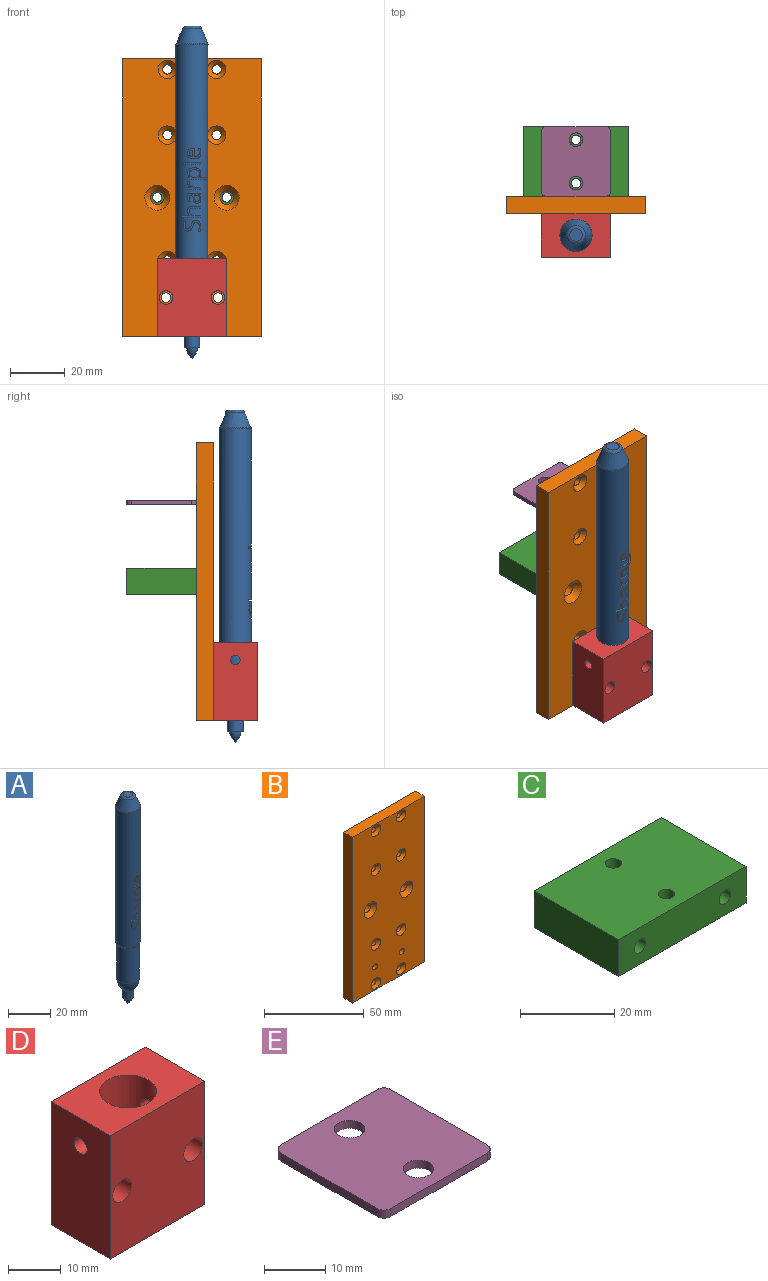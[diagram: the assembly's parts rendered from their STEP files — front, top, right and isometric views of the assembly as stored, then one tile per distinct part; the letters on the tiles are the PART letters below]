
ASSEMBLY  parts=5 mates=5
PART A: 161 faces, bbox 21x21x125.7 mm
  f0: cylinder r=5.87mm len=78.14mm, axis (0,0,-1), area 2809.1mm2, adj f9,f10,f11,f12,f13,f14,f15,f16
  f1: plane 13.84x13.84mm, normal (0,0,-1), area 11.1mm2, adj f2,f7
  f2: revolved ~4.13x2.06mm, area 0mm2, adj f1
  f3: plane 4.64x4.64mm, normal (0,0,1), area 16.9mm2, adj f8
  f4: cone r=5.87mm half-angle=22deg, axis (0,0,-1), area 177.5mm2, adj f8,f9
  f5: cylinder r=5.4mm len=20.32mm, axis (0,0,-1), area 689.1mm2, adj f6,f10
  f6: revolved ~10.8x10.8mm, area 199.6mm2, adj f5,f7
  f7: cylinder r=2.79mm len=5.59mm, axis (0,0,-1), area 83.6mm2, adj f1,f6
  f8: torus R=2.32mm, axis (0,0,1), area 28.3mm2, adj f3,f4
  f9: torus R=4.6mm, axis (0,0,1), area 17.9mm2, adj f0,f4
  f10: torus R=4.6mm, axis (0,0,-1), area 40.8mm2, adj f0,f5
  f11: plane 4.94x0.72mm, normal (-1,0,0), area 3.5mm2, adj f0,f12,f26,f28
  f12: plane 5.87x3.08mm, normal (0,0,-1), area 17.1mm2, adj f0,f11,f13,f26
  f13: extruded ~5.87x1.31mm, area 8.2mm2, adj f0,f12,f14,f26
  f14: extruded ~5.75x1.3mm, area 7.9mm2, adj f0,f13,f15,f26
  f15: extruded ~5.7x0.89mm, area 5.2mm2, adj f0,f14,f16,f26
  f16: extruded ~5.81x0.6mm, area 4.7mm2, adj f0,f15,f17,f26
  f17: plane 5.81x0.04mm, normal (1,0,0), area 0.2mm2, adj f0,f16,f18,f26
  f18: extruded ~5.81x0.61mm, area 3.5mm2, adj f0,f17,f19,f26
  f19: plane 5.68x2.03mm, normal (0,0,-1), area 10.7mm2, adj f0,f18,f20,f26
  f20: plane 4.7x0.72mm, normal (1,0,0), area 3.4mm2, adj f0,f19,f21,f26
  f21: plane 6.7x5.87mm, normal (0,0,1), area 37.1mm2, adj f0,f20,f22,f26
  f22: plane 4.94x0.72mm, normal (-1,0,0), area 3.5mm2, adj f0,f21,f23,f26
  f23: plane 5.83x2.47mm, normal (0,0,-1), area 13.6mm2, adj f0,f22,f24,f26
  f24: extruded ~5.87x1.33mm, area 8.2mm2, adj f0,f23,f25,f26
  f25: extruded ~5.84x1.09mm, area 7mm2, adj f0,f24,f26,f27
  f26: plane 6.7x3.95mm, normal (0,-1,0), area 9.5mm2, adj f11,f12,f13,f14,f15,f16,f17,f18
  f27: extruded ~5.83x0.82mm, area 5.2mm2, adj f0,f25,f26,f29
  f28: plane 5.87x3.05mm, normal (0,0,1), area 17mm2, adj f0,f11,f26,f29
  f29: extruded ~5.87x0.86mm, area 5.4mm2, adj f0,f26,f27,f28
  f30: extruded ~5.71x0.81mm, area 4.9mm2, adj f0,f31,f40,f42
  f31: extruded ~5.84x0.71mm, area 5.5mm2, adj f0,f30,f32,f40
  f32: plane 5.84x0.03mm, normal (1,0,0), area 0.2mm2, adj f0,f31,f33,f40
  f33: plane 5.84x0.87mm, normal (0.09,0,-1), area 5.1mm2, adj f0,f32,f34,f40
  f34: plane 5.67x0.59mm, normal (1,0,0), area 3.3mm2, adj f0,f33,f35,f40
  f35: plane 5.87x4.72mm, normal (0,0,1), area 26.7mm2, adj f0,f34,f36,f40
  f36: plane 4.94x0.72mm, normal (-1,0,0), area 3.5mm2, adj f0,f35,f37,f40
  f37: plane 5.84x2.53mm, normal (0,0,-1), area 13.9mm2, adj f0,f36,f38,f40
  f38: extruded ~5.85x1.16mm, area 7.3mm2, adj f0,f37,f39,f40
  f39: extruded ~5.85x0.98mm, area 6.5mm2, adj f0,f38,f40,f41
  f40: plane 4.81x2.72mm, normal (0,-1,0), area 4.6mm2, adj f30,f31,f32,f33,f34,f35,f36,f37
  f41: extruded ~5.8x0.52mm, area 3mm2, adj f0,f39,f40,f43
  f42: extruded ~5.66x0.56mm, area 3.2mm2, adj f0,f30,f40,f43
  f43: plane 5.8x0.66mm, normal (-0.15,0,-0.99), area 3.8mm2, adj f0,f40,f41,f42
  f44: plane 5.87x4.72mm, normal (0,0,-1), area 26.7mm2, adj f0,f45,f46,f47
  f45: plane 4.72x0.72mm, normal (0,-1,0), area 3.4mm2, adj f44,f46,f47,f48
  f46: plane 5.67x0.72mm, normal (1,0,0), area 4.1mm2, adj f0,f44,f45,f48
  f47: plane 4.94x0.72mm, normal (-1,0,0), area 3.5mm2, adj f0,f44,f45,f48
  f48: plane 5.87x4.72mm, normal (0,0,1), area 26.7mm2, adj f0,f45,f46,f47
  f49: extruded ~5.33x0.36mm, area 2mm2, adj f0,f50,f54,f56
  f50: extruded ~5.39x0.3mm, area 1.8mm2, adj f0,f49,f51,f54
  f51: extruded ~5.39x0.3mm, area 1.8mm2, adj f0,f50,f52,f54
  f52: extruded ~5.33x0.36mm, area 2.1mm2, adj f0,f51,f53,f54
  f53: extruded ~5.15x0.36mm, area 2mm2, adj f0,f52,f54,f55
  f54: plane 0.95x0.84mm, normal (0,-1,0), area 0.7mm2, adj f49,f50,f51,f52,f53,f55,f56,f57
  f55: extruded ~4.94x0.3mm, area 1.6mm2, adj f0,f53,f54,f57
  f56: extruded ~5.15x0.36mm, area 2mm2, adj f0,f49,f54,f57
  f57: extruded ~4.94x0.3mm, area 1.6mm2, adj f0,f54,f55,f56
  f58: extruded ~5.33x0.66mm, area 3.7mm2, adj f59,f79,f81,f86
  f59: extruded ~5.57x0.59mm, area 3.6mm2, adj f58,f60,f79,f86
  f60: extruded ~5.76x0.73mm, area 4.9mm2, adj f59,f61,f79,f86
  f61: extruded ~5.81x1.23mm, area 7.4mm2, adj f60,f62,f79,f86
  f62: plane 5.81x0.72mm, normal (-1,0,-0.04), area 4.2mm2, adj f61,f79,f80,f86
  f63: plane 4.94x0.53mm, normal (-1,0,0), area 2.6mm2, adj f0,f64,f79,f84
  f64: plane 5.87x3.22mm, normal (0,0,-1), area 18mm2, adj f0,f63,f65,f79
  f65: extruded ~5.87x1.2mm, area 7.6mm2, adj f0,f64,f66,f79
  f66: extruded ~5.74x1.25mm, area 7.6mm2, adj f0,f65,f67,f79
  f67: extruded ~5.68x0.83mm, area 4.8mm2, adj f0,f66,f68,f79
  f68: extruded ~5.75x0.76mm, area 4.7mm2, adj f0,f67,f69,f79
  f69: plane 5.84x0.55mm, normal (-0.37,0,0.93), area 3.4mm2, adj f0,f68,f70,f79
  f70: extruded ~5.84x1.33mm, area 8.1mm2, adj f0,f69,f71,f79
  f71: extruded ~5.82x0.77mm, area 4.8mm2, adj f0,f70,f72,f79
  f72: extruded ~5.87x0.82mm, area 5.1mm2, adj f0,f71,f73,f79
  f73: plane 5.87x0.29mm, normal (0,0,1), area 1.7mm2, adj f0,f72,f74,f79
  f74: plane 5.86x0.8mm, normal (1,0,0.03), area 4.7mm2, adj f0,f73,f75,f79
  f75: extruded ~5.86x2.29mm, area 17.8mm2, adj f0,f74,f76,f79
  f76: extruded ~5.57x1.03mm, area 6.1mm2, adj f0,f75,f77,f79
  f77: extruded ~5.11x1.1mm, area 5.9mm2, adj f0,f76,f78,f79
  f78: extruded ~4.99x0.88mm, area 4.4mm2, adj f0,f77,f79,f83
  f79: plane 4.88x3.79mm, normal (0,-1,0), area 8.7mm2, adj f58,f59,f60,f61,f62,f63,f64,f65
  f80: plane 5.81x0.43mm, normal (0,0,1), area 2.5mm2, adj f62,f79,f82,f86
  f81: extruded ~5.4x1.05mm, area 6.1mm2, adj f58,f79,f82,f86
  f82: extruded ~5.73x1.02mm, area 6.3mm2, adj f79,f80,f81,f86
  f83: extruded ~5.31x0.7mm, area 4.8mm2, adj f0,f78,f79,f85
  f84: plane 5.32x0.68mm, normal (-0.21,0,0.98), area 3.5mm2, adj f0,f63,f79,f85
  f85: plane 5.31x0.03mm, normal (-1,0,0), area 0.2mm2, adj f0,f79,f83,f84
  f86: cylinder r=5.87mm len=2.32mm, axis (0,0,-1), area 3.4mm2, adj f58,f59,f60,f61,f62,f80,f81,f82
  f87: extruded ~5.85x0.98mm, area 6.6mm2, adj f88,f106,f108,f113
  f88: extruded ~5.85x1.35mm, area 8.3mm2, adj f87,f89,f106,f113
  f89: extruded ~5.82x1.37mm, area 8.1mm2, adj f88,f90,f106,f113
  f90: extruded ~5.46x0.96mm, area 6mm2, adj f89,f91,f106,f113
  f91: extruded ~5.43x1.06mm, area 6.3mm2, adj f90,f92,f106,f113
  f92: extruded ~5.82x1.42mm, area 8.4mm2, adj f91,f106,f107,f113
  f93: extruded ~5.26x1.44mm, area 8.3mm2, adj f0,f94,f106,f111
  f94: extruded ~5.82x1.81mm, area 10.6mm2, adj f0,f93,f95,f106
  f95: extruded ~5.87x1.8mm, area 11.2mm2, adj f0,f94,f96,f106
  f96: extruded ~5.79x1.45mm, area 9.4mm2, adj f0,f95,f97,f106
  f97: extruded ~5.69x0.84mm, area 4.9mm2, adj f0,f96,f98,f106
  f98: extruded ~5.8x0.64mm, area 5mm2, adj f0,f97,f99,f106
  f99: plane 5.8x0.03mm, normal (1,0,0), area 0.2mm2, adj f0,f98,f100,f106
  f100: plane 5.81x0.65mm, normal (0.15,0,-0.99), area 3.8mm2, adj f0,f99,f101,f106
  f101: plane 5.67x0.58mm, normal (1,0,0), area 3.3mm2, adj f0,f100,f102,f106
  f102: plane 6.84x5.87mm, normal (0,0,1), area 35.1mm2, adj f0,f101,f103,f106
  f103: plane 2.54x0.72mm, normal (-1,0,0), area 1.8mm2, adj f0,f102,f104,f106
  f104: plane 4.82x1.94mm, normal (0,0,-1), area 7.5mm2, adj f0,f103,f105,f106
  f105: extruded ~5.28x0.78mm, area 4mm2, adj f0,f104,f106,f110
  f106: plane 6.93x4.16mm, normal (0,-1,0), area 11mm2, adj f87,f88,f89,f90,f91,f92,f93,f94
  f107: plane 5.84x0.16mm, normal (0,0,-1), area 0.9mm2, adj f92,f106,f109,f113
  f108: extruded ~5.84x1.05mm, area 6.7mm2, adj f87,f106,f109,f113
  f109: extruded ~5.87x1.28mm, area 7.9mm2, adj f106,f107,f108,f113
  f110: plane 5.28x0.05mm, normal (-1,0,0), area 0.3mm2, adj f0,f105,f106,f112
  f111: extruded ~4.99x0.84mm, area 4.3mm2, adj f0,f93,f106,f112
  f112: extruded ~5.28x0.64mm, area 4.3mm2, adj f0,f106,f110,f111
  f113: cylinder r=5.87mm len=3.69mm, axis (0,0,-1), area 8.5mm2, adj f87,f88,f89,f90,f91,f92,f107,f108
  f114: extruded ~5.84x0.86mm, area 5.6mm2, adj f115,f127,f129,f134
  f115: extruded ~5.86x1.04mm, area 6.4mm2, adj f114,f127,f128,f134
  f116: extruded ~4.93x0.82mm, area 4mm2, adj f0,f117,f127,f132
  f117: extruded ~5.08x0.72mm, area 3.8mm2, adj f0,f116,f118,f127
  f118: plane 5.4x0.64mm, normal (0,0,-1), area 3.3mm2, adj f0,f117,f119,f127
  f119: extruded ~5.4x1.51mm, area 8.3mm2, adj f0,f118,f120,f127
  f120: extruded ~5.44x1.12mm, area 6.6mm2, adj f0,f119,f121,f127
  f121: extruded ~5.8x1.26mm, area 7.7mm2, adj f0,f120,f122,f127
  f122: plane 5.8x3.25mm, normal (-1,0,0), area 18.8mm2, adj f0,f121,f123,f127
  f123: plane 5.85x0.45mm, normal (0,0,-1), area 2.6mm2, adj f0,f122,f124,f127
  f124: extruded ~5.85x1.54mm, area 9.7mm2, adj f0,f123,f125,f127
  f125: extruded ~5.78x1.4mm, area 9mm2, adj f0,f124,f126,f127
  f126: extruded ~5.8x1.51mm, area 9.8mm2, adj f0,f125,f127,f131
  f127: plane 4.89x3.99mm, normal (0,-1,0), area 8.9mm2, adj f114,f115,f116,f117,f118,f119,f120,f121
  f128: plane 5.86x2.47mm, normal (1,0,0), area 14.5mm2, adj f115,f127,f130,f134
  f129: extruded ~5.84x0.91mm, area 5.9mm2, adj f114,f127,f130,f134
  f130: extruded ~5.86x1.02mm, area 6.5mm2, adj f127,f128,f129,f134
  f131: extruded ~5.87x1.81mm, area 11.3mm2, adj f0,f126,f127,f133
  f132: extruded ~5.26x1.65mm, area 9.1mm2, adj f0,f116,f127,f133
  f133: extruded ~5.81x1.77mm, area 10.6mm2, adj f0,f127,f131,f132
  f134: cylinder r=5.87mm len=2.47mm, axis (0,0,-1), area 2.7mm2, adj f114,f115,f128,f129,f130
  f135: extruded ~5.86x1.05mm, area 6.6mm2, adj f0,f136,f157,f159
  f136: extruded ~5.87x1.36mm, area 9.2mm2, adj f0,f135,f137,f157
  f137: extruded ~5.87x0.88mm, area 5.6mm2, adj f0,f136,f138,f157
  f138: extruded ~5.83x0.41mm, area 3.3mm2, adj f0,f137,f139,f157
  f139: extruded ~5.77x0.54mm, area 3.2mm2, adj f0,f138,f140,f157
  f140: extruded ~5.65x0.69mm, area 4.4mm2, adj f0,f139,f141,f157
  f141: extruded ~5.4x0.91mm, area 5.1mm2, adj f0,f140,f142,f157
  f142: extruded ~5.43x1.52mm, area 8.4mm2, adj f0,f141,f143,f157
  f143: plane 5.44x0.64mm, normal (-0.34,0,-0.94), area 3.6mm2, adj f0,f142,f144,f157
  f144: extruded ~5.13x1.73mm, area 8.9mm2, adj f0,f143,f145,f157
  f145: extruded ~5.17x1.45mm, area 7.8mm2, adj f0,f144,f146,f157
  f146: extruded ~5.65x1.16mm, area 7.2mm2, adj f0,f145,f147,f157
  f147: extruded ~5.85x1.12mm, area 7mm2, adj f0,f146,f148,f157
  f148: extruded ~5.87x1.25mm, area 8.7mm2, adj f0,f147,f149,f157
  f149: extruded ~5.87x0.94mm, area 6mm2, adj f0,f148,f150,f157
  f150: extruded ~5.84x0.44mm, area 3.4mm2, adj f0,f149,f151,f157
  f151: extruded ~5.78x0.54mm, area 3.2mm2, adj f0,f150,f152,f157
  f152: extruded ~5.66x0.77mm, area 4.9mm2, adj f0,f151,f153,f157
  f153: extruded ~5.39x1.1mm, area 6.1mm2, adj f0,f152,f154,f157
  f154: extruded ~5.3x0.9mm, area 4.8mm2, adj f0,f153,f155,f157
  f155: extruded ~5.42x0.84mm, area 4.7mm2, adj f0,f154,f156,f157
  f156: plane 5.42x0.71mm, normal (0,0,1), area 3.7mm2, adj f0,f155,f157,f158
  f157: plane 6.47x3.96mm, normal (0,-1,0), area 9.2mm2, adj f135,f136,f137,f138,f139,f140,f141,f142
  f158: extruded ~5.07x1.72mm, area 8.7mm2, adj f0,f156,f157,f160
  f159: extruded ~5.68x1.3mm, area 8.1mm2, adj f0,f135,f157,f160
  f160: extruded ~5.17x1.64mm, area 8.6mm2, adj f0,f157,f158,f159
PART B: 28 faces, bbox 50.8x6.4x101.6 mm
  f0: plane 101.6x6.35mm, normal (-1,0,0), area 645.2mm2, adj f1,f3,f4,f5
  f1: plane 50.8x6.35mm, normal (0,0,-1), area 322.6mm2, adj f0,f2,f4,f5
  f2: plane 101.6x6.35mm, normal (1,0,0), area 645.2mm2, adj f1,f3,f4,f5
  f3: plane 50.8x6.35mm, normal (0,0,1), area 322.6mm2, adj f0,f2,f4,f5
  f4: plane 101.6x50.8mm, normal (0,-1,0), area 4728.2mm2, adj f0,f1,f2,f3,f7,f9,f11,f13
  f5: plane 101.6x50.8mm, normal (0,1,0), area 5031mm2, adj f0,f1,f2,f3,f6,f8,f10,f12
  f6: cylinder r=1.7mm len=4.69mm, axis (0,-1,0), area 50.1mm2, adj f5,f7
  f7: cone r=1.7mm half-angle=45deg, axis (0,-1,0), area 37.3mm2, adj f4,f6
  f8: cylinder r=1.7mm len=4.69mm, axis (0,-1,0), area 50.1mm2, adj f5,f9
  f9: cone r=1.7mm half-angle=45deg, axis (0,-1,0), area 37.3mm2, adj f4,f8
  f10: cylinder r=1.7mm len=4.69mm, axis (0,-1,0), area 50.1mm2, adj f5,f11
  f11: cone r=1.7mm half-angle=45deg, axis (0,-1,0), area 37.3mm2, adj f4,f10
  f12: cylinder r=1.7mm len=4.69mm, axis (0,-1,0), area 50.1mm2, adj f5,f13
  f13: cone r=1.7mm half-angle=45deg, axis (0,-1,0), area 37.3mm2, adj f4,f12
  f14: cylinder r=1.7mm len=4.69mm, axis (0,-1,0), area 50.1mm2, adj f5,f15
  f15: cone r=1.7mm half-angle=45deg, axis (0,-1,0), area 37.3mm2, adj f4,f14
  f16: cylinder r=1.7mm len=4.69mm, axis (0,-1,0), area 50.1mm2, adj f5,f17
  f17: cone r=1.7mm half-angle=45deg, axis (0,-1,0), area 37.3mm2, adj f4,f16
  f18: cylinder r=1.7mm len=4.69mm, axis (0,-1,0), area 50.1mm2, adj f5,f19
  f19: cone r=1.7mm half-angle=45deg, axis (0,-1,0), area 37.3mm2, adj f4,f18
  f20: cylinder r=1.7mm len=4.69mm, axis (0,-1,0), area 50.1mm2, adj f5,f21
  f21: cone r=1.7mm half-angle=45deg, axis (0,-1,0), area 37.3mm2, adj f4,f20
  f22: cylinder r=2.49mm len=4.98mm, axis (0,-1,0), area 62.1mm2, adj f5,f23
  f23: cone r=2.49mm half-angle=41deg, axis (0,-1,0), area 69.9mm2, adj f4,f22
  f24: cylinder r=2.49mm len=4.98mm, axis (0,-1,0), area 62.1mm2, adj f5,f25
  f25: cone r=2.49mm half-angle=41deg, axis (0,-1,0), area 69.9mm2, adj f4,f24
  f26: cylinder r=1.73mm len=6.35mm, axis (0,-1,0), area 68.9mm2, adj f4,f5
  f27: cylinder r=1.73mm len=6.35mm, axis (0,-1,0), area 68.9mm2, adj f4,f5
PART C: 10 faces, bbox 38.1x25.4x9.5 mm
  f0: plane 25.4x9.53mm, normal (-1,0,0), area 241.9mm2, adj f1,f3,f4,f5
  f1: plane 38.1x25.4mm, normal (0,0,-1), area 949mm2, adj f0,f2,f4,f5,f8,f9
  f2: plane 25.4x9.53mm, normal (1,0,0), area 241.9mm2, adj f1,f3,f4,f5
  f3: plane 38.1x25.4mm, normal (0,0,1), area 949mm2, adj f0,f2,f4,f5,f8,f9
  f4: plane 38.1x9.53mm, normal (0,-1,0), area 344.2mm2, adj f0,f1,f2,f3,f6,f7
  f5: plane 38.1x9.53mm, normal (0,1,0), area 344.2mm2, adj f0,f1,f2,f3,f6,f7
  f6: cylinder r=1.73mm len=25.4mm, axis (0,-1,0), area 275.6mm2, adj f4,f5
  f7: cylinder r=1.73mm len=25.4mm, axis (0,-1,0), area 275.6mm2, adj f4,f5
  f8: cylinder r=1.73mm len=9.53mm, axis (0,0,1), area 103.4mm2, adj f1,f3
  f9: cylinder r=1.73mm len=9.53mm, axis (0,0,1), area 103.4mm2, adj f1,f3
PART D: 11 faces, bbox 25.4x15.9x28.6 mm
  f0: cylinder r=1.73mm len=7.59mm, axis (1,0,0), area 80.8mm2, adj f1,f8
  f1: plane 28.58x15.88mm, normal (-1,0,0), area 444.3mm2, adj f0,f2,f4,f5,f6
  f2: plane 28.58x25.4mm, normal (0,-1,0), area 686.9mm2, adj f1,f3,f5,f6,f9,f10
  f3: plane 28.58x15.88mm, normal (1,0,0), area 444.3mm2, adj f2,f4,f5,f6,f7
  f4: plane 28.58x25.4mm, normal (0,1,0), area 686.9mm2, adj f1,f3,f5,f6,f9,f10
  f5: plane 25.4x15.88mm, normal (0,0,1), area 311.7mm2, adj f1,f2,f3,f4,f8
  f6: plane 25.4x15.88mm, normal (0,0,-1), area 311.7mm2, adj f1,f2,f3,f4,f8
  f7: cylinder r=1.73mm len=7.59mm, axis (1,0,0), area 80.8mm2, adj f3,f8
  f8: cylinder r=5.4mm len=28.58mm, axis (0,0,1), area 950.1mm2, adj f0,f5,f6,f7
  f9: cylinder r=2.49mm len=15.88mm, axis (0,-1,0), area 248.3mm2, adj f2,f4
  f10: cylinder r=2.49mm len=15.88mm, axis (0,-1,0), area 248.3mm2, adj f2,f4
PART E: 12 faces, bbox 25.4x25.4x1.6 mm
  f0: plane 22.23x1.59mm, normal (-1,0,0), area 35.3mm2, adj f4,f5,f8,f11
  f1: plane 22.23x1.59mm, normal (0,-1,0), area 35.3mm2, adj f4,f5,f8,f9
  f2: plane 22.23x1.59mm, normal (1,0,0), area 35.3mm2, adj f4,f5,f9,f10
  f3: plane 22.23x1.59mm, normal (0,1,0), area 35.3mm2, adj f4,f5,f10,f11
  f4: plane 25.4x25.4mm, normal (0,0,1), area 604.1mm2, adj f0,f1,f2,f3,f6,f7,f8,f9
  f5: plane 25.4x25.4mm, normal (0,0,-1), area 604.1mm2, adj f0,f1,f2,f3,f6,f7,f8,f9
  f6: cylinder r=2.49mm len=4.98mm, axis (0,0,1), area 24.8mm2, adj f4,f5
  f7: cylinder r=2.49mm len=4.98mm, axis (0,0,1), area 24.8mm2, adj f4,f5
  f8: cylinder r=1.59mm len=1.59mm, axis (0,0,1), area 4mm2, adj f0,f1,f4,f5
  f9: cylinder r=1.59mm len=1.59mm, axis (0,0,-1), area 4mm2, adj f1,f2,f4,f5
  f10: cylinder r=1.59mm len=1.59mm, axis (0,0,1), area 4mm2, adj f2,f3,f4,f5
  f11: cylinder r=1.59mm len=1.59mm, axis (0,0,-1), area 4mm2, adj f0,f3,f4,f5
PLACE A t=(-25.4,6.35,-53.21)mm
PLACE B rot(axis=(0,0.54,-0.84),0deg) t=(-25.4,6.35,-50.94)mm
PLACE C rot(axis=(0,0,1),180deg) t=(19.05,6.35,-4.77)mm
PLACE D t=(-25.4,6.35,-50.94)mm
PLACE E rot(axis=(0,0,1),180deg) t=(0,19.05,28.03)mm
MATE fastened B.f26 <-> D.f9  axis (0,-1,0) through (9.53,0,-36.66)mm
MATE cylindrical C.f8 <-> E.f7  axis (0,0,1) through (0,26.99,4.75)mm
MATE fastened A.f0 <-> D.f8  axis (0,0,-1) through (0,-7.94,-22.37)mm
MATE cylindrical C.f9 <-> E.f6  axis (0,0,1) through (0,11.11,4.75)mm
MATE fastened C.f5 <-> B.f5  axis (0,-1,0) through (0,6.35,-0.01)mm
